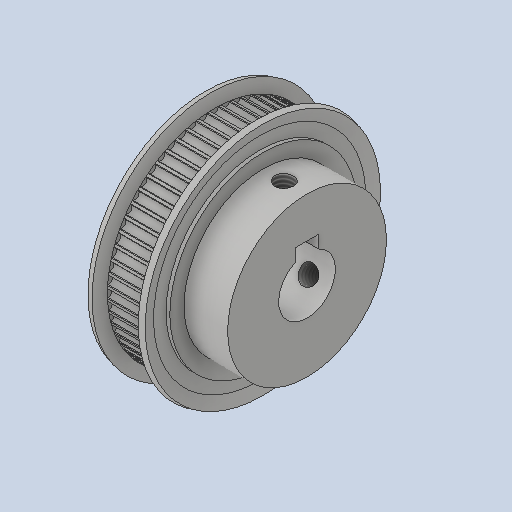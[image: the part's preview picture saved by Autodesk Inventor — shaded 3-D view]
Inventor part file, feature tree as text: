
AUTODESK INVENTOR PART (.ipt)
format: ipt  version: 2023 (Build 270158000, 158)  size: 601,600 bytes
history: native  units: mm
features: other x14, sketch x7, revolve x5, extrude x2, thread x2, pattern_circular x1
ambient origin geometry x8: Origin, YZ Plane, XZ Plane, XY Plane, X Axis, Y Axis, Z Axis, Center Point
bodies: Solid1 (feature_tree)
feature tree (31):
  revolve  "Revolution1"  [1 undecoded]
  extrude  "Extrusion1"  TaperAngle=360.0deg  [1 undecoded]
  pattern_circular  "Circular Pattern1"  [2 undecoded]
  revolve  "Revolution2"  [1 undecoded]
  revolve  "Revolution3"  [1 undecoded]
  revolve  "Revolution4"  [1 undecoded]
  thread  "Thread1"  [1 undecoded]
  revolve  "Revolution5"  [1 undecoded]
  thread  "Thread2"  [1 undecoded]
  extrude  "Extrusion2"  [1 undecoded]
  other  "to_screw_B1_XY"
  other  "to_screw_B1_YZ"
  other  "to_screw_B1_ZX"
  other  "to_screw_B1_X"
  other  "to_screw_B1_Y"
  other  "to_screw_B1_Z"
  other  "to_screw_B1_Center"
  other  "to_screw_B2_XY"
  other  "to_screw_B2_YZ"
  other  "to_screw_B2_ZX"
  other  "to_screw_B2_X"
  other  "to_screw_B2_Y"
  other  "to_screw_B2_Z"
  other  "to_screw_B2_Center"
  sketch  "Sketch_17"  dims[d8=360.0deg]
  sketch  "Sketch_18"  dims[d9=7.2mm d10=0.0mm]
  sketch  "Sketch_20"  dims[d11=360.0deg]
  sketch  "Sketch_21"  dims[d12=9.0mm d13=0.0mm d14=18.0mm d15=0.0mm d16=0.0mm]
  sketch  "Sketch_1"  dims[d0=360.0deg d1=7.0mm d2=0.0mm]
  sketch  "Sketch_2"  dims[d3=600.0mm d4=1.047198mm d6=360.0deg]
  sketch  "Sketch_3"  dims[d7=360.0deg]
note: 11 required parameter values undecoded (feature->parameter linkage not recoverable at this tier; creation-order binding heuristic only, values carry confidence <= 0.55)